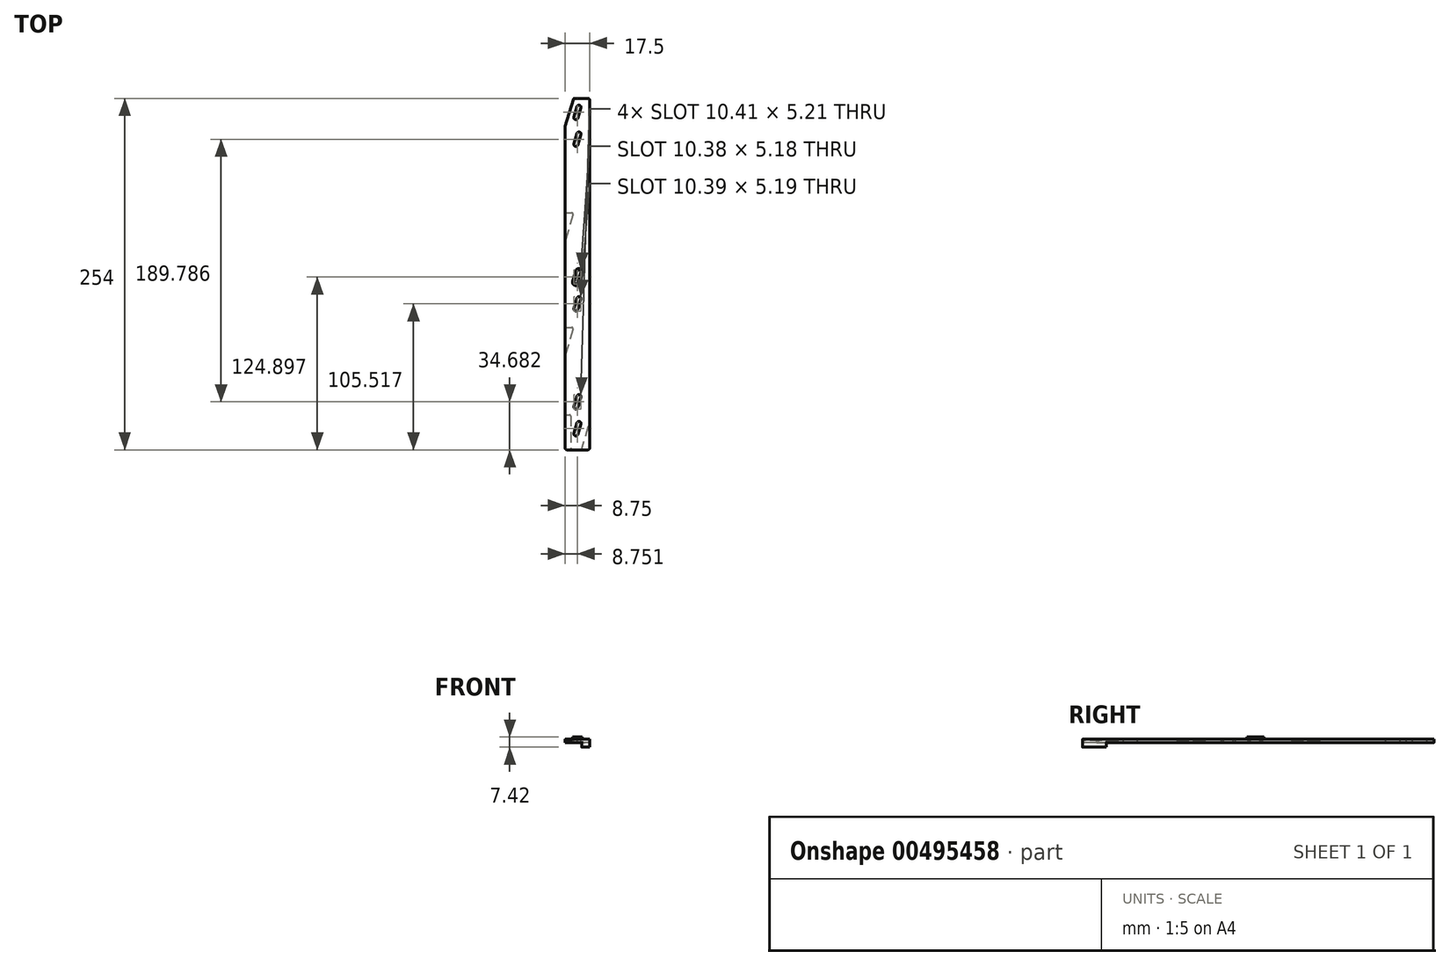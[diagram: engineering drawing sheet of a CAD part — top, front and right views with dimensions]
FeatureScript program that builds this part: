
annotation { "Feature Type Name" : "Feature", "Feature Type Description" : "" }
export const myFeature = defineFeature(function(context is Context, id is Id, definition is map)
    precondition{}
    {
        {
            var Q0;
            Q0=qCreatedBy(makeId("Top.planeOp"),FACE);
            var sketch = newSketch(context, id + "F0", { "sketchPlane" : qUnion([Q0])});
            skLineSegment(sketch, "E0.bottom", {"start": v(-2.75, 106.97) * mm, "end": v(8.75, 106.97) * mm});
            skLineSegment(sketch, "E0.left", {"start": v(-8.75, 86.96) * mm, "end": v(-8.75, -147.03) * mm});
            skLineSegment(sketch, "E0.right", {"start": v(8.75, 106.97) * mm, "end": v(8.75, -147.03) * mm});
            skLineSegment(sketch, "E1", {"start": v(-2.75, 106.97) * mm, "end": v(-8.75, 86.96) * mm});
            skLineSegment(sketch, "E2", {"start": v(-8.75, -147.03) * mm, "end": v(8.75, -147.03) * mm});
            skLineSegment(sketch, "E3", {"start": v(3, 106.97) * mm, "end": v(-14.54, 106.97) * mm, "construction": true});
            skLineSegment(sketch, "E4", {"start": v(-8.75, 86.96) * mm, "end": v(-8.75, 113.53) * mm, "construction": true});
            skSolve(sketch);
        }
        {
            var Q0;
            Q0=makeQuery(id+"F0.imprint","IMPRINT",FACE,{"disambiguationData":[TD([[makeQuery(id+"F0.imprint","IMPRINT",EDGE,{"derivedFrom":sQuery(id+"F0.wireOp",EDGE,"E0.bottom")}),-1.0]])]});
            var Q1;
            {var subQ0=sQuery(id+"F0.wireOp",EDGE,"633dc75a-0e58-463e-8379-161fb5928875");Q1=makeQuery(id+"F0.imprint","IMPRINT",FACE,{"disambiguationData":[TD([[makeQuery(id+"F0.imprint","IMPRINT",EDGE,{"derivedFrom":subQ0}),1.0]])]});}
            var Q2;
            {var subQ0=sQuery(id+"F0.wireOp",EDGE,"2a0ce6a0-4d5f-4fe7-96eb-a293c719060f");Q2=makeQuery(id+"F0.imprint","IMPRINT",FACE,{"disambiguationData":[TD([[makeQuery(id+"F0.imprint","IMPRINT",EDGE,{"derivedFrom":subQ0}),1.0]])]});}
            var Q3;
            {var subQ2=sQuery(id+"F0.wireOp",EDGE,"24cbd44b-3bb7-44ab-ab79-63d6f2c5d095");Q3=makeQuery(id+"F0.imprint","IMPRINT",FACE,{"disambiguationData":[TD([[makeQuery(id+"F0.imprint","IMPRINT",EDGE,{"derivedFrom":subQ2}),-1.0]])]});}
            var Q4;
            Q4=makeQuery(id+"F0.imprint","IMPRINT",FACE,{"disambiguationData":[TD([[makeQuery(id+"F0.imprint","IMPRINT",EDGE,{"derivedFrom":sQuery(id+"F0.wireOp",EDGE,"be87b283-c7b7-44dc-804c-dedf415bc6b7")}),1.0]])]});
            extrude(context, id + "F1", {"entities" : qUnion([Q0, Q1, Q2, Q3, Q4]), "oppositeDirection" : true, "depth" : 4.25 * mm});
        }
        {
            var Q0;
            Q0=makeQuery(id+"F1.opExtrude","CAP_FACE",FACE,{"disambiguationData":[OSD([sQuery(id+"F0.wireOp",EDGE,"E0.bottom"),sQuery(id+"F0.wireOp",EDGE,"E0.top"),sQuery(id+"F0.wireOp",EDGE,"E0.left"),sQuery(id+"F0.wireOp",EDGE,"E0.right"),sQuery(id+"F0.wireOp",EDGE,"10f6f7c6-98f3-4bf4-98ed-882440dcabe1"),sQuery(id+"F0.wireOp",EDGE,"E1"),sQuery(id+"F0.wireOp",EDGE,"7971e424-7568-4981-839e-3620bab7779a.trimOffspring"),sQuery(id+"F0.wireOp",EDGE,"998ecffa-0773-4704-a632-2820b9788bde.trimOffspring"),sQuery(id+"F0.wireOp",EDGE,"E2"),sQuery(id+"F0.wireOp",EDGE,"j7FGSntq-Wqsv-4P9R-nEKO-KN23OMY3wqPX"),sQuery(id+"F0.wireOp",EDGE,"27ecc4d9-ff6f-4d39-984e-df0c997e4436")])],"isStart":false});
            var sketch = newSketch(context, id + "F2", { "sketchPlane" : qUnion([Q0])});
            skLineSegment(sketch, "E5", {"start": v(-8.75, -24.19) * mm, "end": v(-2.75, -24.19) * mm});
            skLineSegment(sketch, "E6", {"start": v(-2.75, -24.19) * mm, "end": v(-8.75, -4.18) * mm});
            skLineSegment(sketch, "E7", {"start": v(-4.85, 147.03) * mm, "end": v(-8.75, 147.03) * mm});
            skLineSegment(sketch, "E8.trimOffspring", {"start": v(-8.75, 58.6) * mm, "end": v(-8.75, 78.6) * mm});
            skLineSegment(sketch, "E9.trimOffspring", {"start": v(-8.75, -24.19) * mm, "end": v(-8.75, -4.18) * mm});
            skLineSegment(sketch, "E10", {"start": v(-8.75, 58.6) * mm, "end": v(-2.75, 58.6) * mm});
            skLineSegment(sketch, "E11", {"start": v(-2.75, 58.6) * mm, "end": v(-8.75, 78.6) * mm});
            skLineSegment(sketch, "E12", {"start": v(-8.75, 147.03) * mm, "end": v(-8.75, 121.63) * mm});
            skLineSegment(sketch, "E13", {"start": v(-8.75, 121.63) * mm, "end": v(-4.85, 121.63) * mm});
            skLineSegment(sketch, "E14", {"start": v(-4.85, 121.63) * mm, "end": v(-4.85, 147.03) * mm});
            skLineSegment(sketch, "E15", {"start": v(-173.03, 57.3) * mm, "end": v(-173.03, 57.3) * mm});
            skLineSegment(sketch, "E16", {"start": v(8.75, 127.03) * mm, "end": v(2.75, 147.03) * mm});
            skLineSegment(sketch, "E17", {"start": v(2.75, 147.03) * mm, "end": v(8.75, 147.03) * mm});
            skLineSegment(sketch, "E18", {"start": v(8.75, 147.03) * mm, "end": v(8.75, 127.03) * mm});
            skSolve(sketch);
        }
        {
            var Q0;
            Q0=makeQuery(id+"F2.imprint","IMPRINT",FACE,{"disambiguationData":[TD([[makeQuery(id+"F2.imprint","IMPRINT",EDGE,{"derivedFrom":sQuery(id+"F2.wireOp",EDGE,"E12")}),-1.0]])]});
            var Q1;
            Q1=makeQuery(id+"F2.imprint","IMPRINT",FACE,{"disambiguationData":[TD([[makeQuery(id+"F2.imprint","IMPRINT",EDGE,{"derivedFrom":sQuery(id+"F2.wireOp",EDGE,"E8.trimOffspring")}),-1.0]])]});
            var Q2;
            Q2=makeQuery(id+"F2.imprint","IMPRINT",FACE,{"disambiguationData":[TD([[makeQuery(id+"F2.imprint","IMPRINT",EDGE,{"derivedFrom":sQuery(id+"F2.wireOp",EDGE,"E5")}),1.0]])]});
            extrude(context, id + "F3", {"entities" : qUnion([Q0, Q1, Q2]), "operationType" : NewBodyOperationType.REMOVE, "oppositeDirection" : true, "depth" : 1.7 * mm});
        }
        {
            var Q0;
            Q0=makeQuery(id+"F2.imprint","IMPRINT",FACE,{"disambiguationData":[TD([[makeQuery(id+"F2.imprint","IMPRINT",EDGE,{"derivedFrom":sQuery(id+"F2.wireOp",EDGE,"E16")}),-1.0]])]});
            extrude(context, id + "F4", {"entities" : qUnion([Q0]), "operationType" : NewBodyOperationType.ADD, "depth" : 3.17 * mm});
        }
        {
            var Q0;
            Q0=makeQuery(id+"F3.boolean.opBoolean","COPY",EDGE,{"derivedFrom":makeQuery(id+"F3.opExtrude","SWEPT_EDGE",EDGE,{"disambiguationData":[OSD([sQuery(id+"F2.wireOp",EDGE,"E10"),sQuery(id+"F2.wireOp",EDGE,"E11")])]})});
            var Q1;
            Q1=makeQuery(id+"F3.boolean.opBoolean","COPY",EDGE,{"derivedFrom":makeQuery(id+"F3.opExtrude","SWEPT_EDGE",EDGE,{"disambiguationData":[OSD([sQuery(id+"F0.wireOp",EDGE,"E0.left"),sQuery(id+"F2.wireOp",EDGE,"E8.trimOffspring"),sQuery(id+"F2.wireOp",EDGE,"E10")])]})});
            var Q2;
            Q2=makeQuery(id+"F3.boolean.opBoolean","COPY",EDGE,{"derivedFrom":makeQuery(id+"F3.opExtrude","SWEPT_EDGE",EDGE,{"disambiguationData":[OSD([sQuery(id+"F2.wireOp",EDGE,"E13"),sQuery(id+"F2.wireOp",EDGE,"E14")])]})});
            var Q3;
            Q3=makeQuery(id+"F3.boolean.opBoolean","COPY",EDGE,{"derivedFrom":makeQuery(id+"F3.opExtrude","SWEPT_EDGE",EDGE,{"disambiguationData":[OSD([sQuery(id+"F0.wireOp",EDGE,"E0.left"),sQuery(id+"F2.wireOp",EDGE,"E12"),sQuery(id+"F2.wireOp",EDGE,"E13")])]})});
            var Q4;
            Q4=makeQuery(id+"F3.boolean.opBoolean","COPY",EDGE,{"derivedFrom":makeQuery(id+"F3.opExtrude","SWEPT_EDGE",EDGE,{"disambiguationData":[OSD([sQuery(id+"F0.wireOp",EDGE,"E2"),sQuery(id+"F2.wireOp",EDGE,"E14"),sQuery(id+"F2.wireOp",EDGE,"E7")])]})});
            var Q5;
            Q5=makeQuery(id+"F1.opExtrude","SWEPT_EDGE",EDGE,{"disambiguationData":[OSD([sQuery(id+"F0.wireOp",EDGE,"E0.left"),sQuery(id+"F0.wireOp",EDGE,"E2")])]});
            var Q6;
            Q6=makeQuery(id+"F4.boolean.opBoolean","MERGE",EDGE,{"derivedFrom":[makeQuery(id+"F1.opExtrude","SWEPT_EDGE",EDGE,{"disambiguationData":[OSD([sQuery(id+"F0.wireOp",EDGE,"E0.right"),sQuery(id+"F0.wireOp",EDGE,"E2")])]}),makeQuery(id+"F4.opExtrude","SWEPT_EDGE",EDGE,{"disambiguationData":[OSD([sQuery(id+"F2.wireOp",EDGE,"E17"),sQuery(id+"F2.wireOp",EDGE,"E18")])]})]});
            var Q7;
            Q7=makeQuery(id+"F4.opExtrude","SWEPT_EDGE",EDGE,{"disambiguationData":[OSD([sQuery(id+"F0.wireOp",EDGE,"E2"),sQuery(id+"F2.wireOp",EDGE,"E16"),sQuery(id+"F2.wireOp",EDGE,"E17")])]});
            var Q8;
            Q8=makeQuery(id+"F3.boolean.opBoolean","COPY",EDGE,{"derivedFrom":makeQuery(id+"F3.opExtrude","SWEPT_EDGE",EDGE,{"disambiguationData":[OSD([sQuery(id+"F2.wireOp",EDGE,"E5"),sQuery(id+"F2.wireOp",EDGE,"E6")])]})});
            var Q9;
            Q9=makeQuery(id+"F3.boolean.opBoolean","COPY",EDGE,{"derivedFrom":makeQuery(id+"F3.opExtrude","SWEPT_EDGE",EDGE,{"disambiguationData":[OSD([sQuery(id+"F0.wireOp",EDGE,"E0.left"),sQuery(id+"F2.wireOp",EDGE,"E5"),sQuery(id+"F2.wireOp",EDGE,"E9.trimOffspring")])]})});
            var Q10;
            Q10=makeQuery(id+"F1.opExtrude","SWEPT_EDGE",EDGE,{"disambiguationData":[OSD([sQuery(id+"F0.wireOp",EDGE,"E0.bottom"),sQuery(id+"F0.wireOp",EDGE,"10f6f7c6-98f3-4bf4-98ed-882440dcabe1")])]});
            var Q11;
            Q11=makeQuery(id+"F1.opExtrude","SWEPT_EDGE",EDGE,{"disambiguationData":[OSD([sQuery(id+"F0.wireOp",EDGE,"E0.bottom"),sQuery(id+"F0.wireOp",EDGE,"E0.right")])]});
            fillet(context, id + "F5", {"entities" : qUnion([Q0, Q1, Q2, Q3, Q4, Q5, Q6, Q7, Q8, Q9, Q10, Q11]), "radius" : 1 * mm, "tangentPropagation" : true, "allowEdgeOverflow" : false});
        }
        {
            var Q0;
            Q0=makeQuery(id+"F4.opExtrude","SWEPT_EDGE",EDGE,{"disambiguationData":[OSD([sQuery(id+"F0.wireOp",EDGE,"E0.right"),sQuery(id+"F2.wireOp",EDGE,"E16"),sQuery(id+"F2.wireOp",EDGE,"E18")])]});
            fillet(context, id + "F6", {"entities" : qUnion([Q0]), "radius" : .5 * mm, "tangentPropagation" : true, "allowEdgeOverflow" : false});
        }
        {
            var Q0;
            Q0=makeQuery(id+"F0.imprint","IMPRINT",FACE,{"disambiguationData":[TD([[makeQuery(id+"F0.imprint","IMPRINT",EDGE,{"derivedFrom":sQuery(id+"F0.wireOp",EDGE,"E0.bottom")}),-1.0]])]});
            var sketch = newSketch(context, id + "F7", { "sketchPlane" : qUnion([Q0])});
            skPoint(sketch, "E19.startSnap0", {"position": v(2.87, 106.97) * mm});
            skLineSegment(sketch, "E20", {"start": v(0, 106.97) * mm, "end": v(0, -147.03) * mm, "construction": true});
            skLineSegment(sketch, "E21.MirrorCS", {"start": v(0.32, 92.68) * mm, "end": v(2.55, 100.1) * mm});
            skLineSegment(sketch, "E22.MirrorCS", {"start": v(-3.5, 93.83) * mm, "end": v(-1.28, 101.25) * mm});
            skLineSegment(sketch, "E23.MirrorCS", {"start": v(1.28, 92.4) * mm, "end": v(3.5, 99.82) * mm});
            skArc(sketch, "E24.MirrorCS", {"start": v(-2.55, 93.54) * mm, "mid": v(-1.54, 91.67) * mm, "end": v(0.32, 92.68) * mm});
            skLineSegment(sketch, "E25.MirrorCS", {"start": v(-2.55, 93.54) * mm, "end": v(-0.32, 100.97) * mm});
            skArc(sketch, "E26.MirrorCS", {"start": v(3.5, 99.82) * mm, "mid": v(1.83, 102.93) * mm, "end": v(-1.28, 101.25) * mm});
            skArc(sketch, "E27.MirrorCS", {"start": v(2.55, 100.1) * mm, "mid": v(1.54, 101.97) * mm, "end": v(-0.32, 100.97) * mm});
            skArc(sketch, "E28.MirrorCS", {"start": v(-3.5, 93.83) * mm, "mid": v(-1.83, 90.72) * mm, "end": v(1.28, 92.4) * mm});
            skArc(sketch, "E29.MirrorCS", {"start": v(1.32, -26.42) * mm, "mid": v(-1.7, -28.28) * mm, "end": v(-3.55, -25.27) * mm});
            skLineSegment(sketch, "E30.MirrorCS", {"start": v(-2.58, -25.52) * mm, "end": v(-0.35, -18.1) * mm});
            skLineSegment(sketch, "E31.MirrorCS", {"start": v(-3.55, -25.27) * mm, "end": v(-1.32, -17.84) * mm});
            skArc(sketch, "E32.MirrorCS", {"start": v(3.55, -19) * mm, "mid": v(1.7, -15.99) * mm, "end": v(-1.32, -17.84) * mm});
            skArc(sketch, "E33.MirrorCS", {"start": v(-2.58, -25.52) * mm, "mid": v(-1.44, -27.3) * mm, "end": v(0.35, -26.17) * mm});
            skArc(sketch, "E34.MirrorCS", {"start": v(2.58, -18.74) * mm, "mid": v(1.44, -16.96) * mm, "end": v(-0.35, -18.1) * mm});
            skLineSegment(sketch, "E35", {"start": v(-1.11, -25.84) * mm, "end": v(1.11, -18.42) * mm, "construction": true});
            skLineSegment(sketch, "E36.MirrorCS", {"start": v(-3.55, -44.65) * mm, "end": v(-1.32, -37.23) * mm});
            skArc(sketch, "E37.MirrorCS", {"start": v(2.57, -38.15) * mm, "mid": v(1.5, -36.36) * mm, "end": v(-0.32, -37.38) * mm});
            skLineSegment(sketch, "E38.MirrorCS", {"start": v(1.32, -45.8) * mm, "end": v(3.55, -38.39) * mm});
            skLineSegment(sketch, "E39.MirrorCS", {"start": v(0.35, -45.58) * mm, "end": v(2.57, -38.15) * mm});
            skArc(sketch, "E40.MirrorCS", {"start": v(3.55, -38.39) * mm, "mid": v(1.7, -35.37) * mm, "end": v(-1.32, -37.23) * mm});
            skArc(sketch, "E41.MirrorCS", {"start": v(-3.55, -44.65) * mm, "mid": v(-1.7, -47.66) * mm, "end": v(1.32, -45.8) * mm});
            skLineSegment(sketch, "E42.MirrorCS", {"start": v(-2.57, -44.88) * mm, "end": v(-0.32, -37.38) * mm});
            skArc(sketch, "E43.MirrorCS", {"start": v(-2.57, -44.88) * mm, "mid": v(-1.46, -46.69) * mm, "end": v(0.35, -45.58) * mm});
            skLineSegment(sketch, "E44", {"start": v(-1.11, -45.23) * mm, "end": v(1.11, -37.8) * mm, "construction": true});
            skArc(sketch, "E45.MirrorCS", {"start": v(2.55, -109.07) * mm, "mid": v(1.54, -107.2) * mm, "end": v(-0.32, -108.2) * mm});
            skArc(sketch, "E46.MirrorCS", {"start": v(-2.55, -115.63) * mm, "mid": v(-1.54, -117.5) * mm, "end": v(0.32, -116.5) * mm});
            skLineSegment(sketch, "E47.MirrorCS", {"start": v(-3.5, -115.34) * mm, "end": v(-1.28, -107.92) * mm});
            skLineSegment(sketch, "E48.MirrorCS", {"start": v(0.32, -116.5) * mm, "end": v(2.55, -109.07) * mm});
            skLineSegment(sketch, "E49.MirrorCS", {"start": v(1.28, -116.78) * mm, "end": v(3.5, -109.35) * mm});
            skLineSegment(sketch, "E50.MirrorCS", {"start": v(-2.55, -115.63) * mm, "end": v(-0.32, -108.2) * mm});
            skArc(sketch, "E51.MirrorCS", {"start": v(3.5, -109.35) * mm, "mid": v(1.83, -106.24) * mm, "end": v(-1.28, -107.92) * mm});
            skArc(sketch, "E52.MirrorCS", {"start": v(-3.5, -115.34) * mm, "mid": v(-1.83, -118.45) * mm, "end": v(1.28, -116.78) * mm});
            skLineSegment(sketch, "E53", {"start": v(-1.11, -116.06) * mm, "end": v(1.11, -108.64) * mm, "construction": true});
            skLineSegment(sketch, "E54", {"start": v(-1.11, 93.11) * mm, "end": v(1.11, 100.53) * mm, "construction": true});
            skArc(sketch, "E55.MirrorCS", {"start": v(-3.5, -134.72) * mm, "mid": v(-1.8, -137.85) * mm, "end": v(1.3, -136.1) * mm});
            skArc(sketch, "E56.MirrorCS", {"start": v(-2.56, -135.05) * mm, "mid": v(-1.55, -136.88) * mm, "end": v(0.3, -135.92) * mm});
            skLineSegment(sketch, "E57.MirrorCS", {"start": v(-3.5, -134.72) * mm, "end": v(-1.28, -127.3) * mm});
            skLineSegment(sketch, "E58.MirrorCS", {"start": v(-2.56, -135.05) * mm, "end": v(-0.33, -127.63) * mm});
            skLineSegment(sketch, "E59.MirrorCS", {"start": v(1.3, -136.1) * mm, "end": v(3.53, -128.68) * mm});
            skLineSegment(sketch, "E60.MirrorCS", {"start": v(0.3, -135.92) * mm, "end": v(2.54, -128.5) * mm});
            skArc(sketch, "E61.MirrorCS", {"start": v(3.53, -128.68) * mm, "mid": v(1.8, -125.62) * mm, "end": v(-1.28, -127.3) * mm});
            skArc(sketch, "E62.MirrorCS", {"start": v(2.54, -128.5) * mm, "mid": v(1.55, -126.58) * mm, "end": v(-0.33, -127.63) * mm});
            skLineSegment(sketch, "E63", {"start": v(1.11, -128.02) * mm, "end": v(-1.11, -135.44) * mm, "construction": true});
            skLineSegment(sketch, "E64", {"start": v(0.35, -26.17) * mm, "end": v(2.58, -18.74) * mm});
            skLineSegment(sketch, "E65", {"start": v(1.32, -26.42) * mm, "end": v(3.55, -19) * mm});
            skLineSegment(sketch, "E66.MirrorCS", {"start": v(0.32, 73.3) * mm, "end": v(2.55, 80.72) * mm});
            skLineSegment(sketch, "E67.MirrorCS", {"start": v(-3.5, 74.45) * mm, "end": v(-1.28, 81.87) * mm});
            skLineSegment(sketch, "E68.MirrorCS", {"start": v(1.28, 73) * mm, "end": v(3.5, 80.43) * mm});
            skArc(sketch, "E69.MirrorCS", {"start": v(-2.55, 74.16) * mm, "mid": v(-1.54, 72.3) * mm, "end": v(0.32, 73.3) * mm});
            skLineSegment(sketch, "E70.MirrorCS", {"start": v(-2.55, 74.16) * mm, "end": v(-0.32, 81.58) * mm});
            skArc(sketch, "E71.MirrorCS", {"start": v(3.5, 80.43) * mm, "mid": v(1.83, 83.54) * mm, "end": v(-1.28, 81.87) * mm});
            skArc(sketch, "E72.MirrorCS", {"start": v(2.55, 80.72) * mm, "mid": v(1.54, 82.59) * mm, "end": v(-0.32, 81.58) * mm});
            skArc(sketch, "E73.MirrorCS", {"start": v(-3.5, 74.45) * mm, "mid": v(-1.83, 71.33) * mm, "end": v(1.28, 73) * mm});
            skLineSegment(sketch, "E74", {"start": v(-1.11, 73.73) * mm, "end": v(1.11, 81.15) * mm, "construction": true});
            skSolve(sketch);
        }
        {
            var Q0;
            Q0=makeQuery(id+"F7.imprint","IMPRINT",FACE,{"disambiguationData":[TD([[makeQuery(id+"F7.imprint","IMPRINT",EDGE,{"derivedFrom":sQuery(id+"F7.wireOp",EDGE,"E21.MirrorCS")}),-1.0]])]});
            var Q1;
            Q1=makeQuery(id+"F7.imprint","IMPRINT",FACE,{"disambiguationData":[TD([[makeQuery(id+"F7.imprint","IMPRINT",EDGE,{"derivedFrom":sQuery(id+"F7.wireOp",EDGE,"E66.MirrorCS")}),-1.0]])]});
            var Q2;
            Q2=makeQuery(id+"F7.imprint","IMPRINT",FACE,{"disambiguationData":[TD([[makeQuery(id+"F7.imprint","IMPRINT",EDGE,{"derivedFrom":sQuery(id+"F7.wireOp",EDGE,"E36.MirrorCS")}),-1.0]])]});
            var Q3;
            Q3=makeQuery(id+"F7.imprint","IMPRINT",FACE,{"disambiguationData":[TD([[makeQuery(id+"F7.imprint","IMPRINT",EDGE,{"derivedFrom":sQuery(id+"F7.wireOp",EDGE,"E29.MirrorCS")}),-1.0]])]});
            var Q4;
            Q4=makeQuery(id+"F7.imprint","IMPRINT",FACE,{"disambiguationData":[TD([[makeQuery(id+"F7.imprint","IMPRINT",EDGE,{"derivedFrom":sQuery(id+"F7.wireOp",EDGE,"E45.MirrorCS")}),-1.0]])]});
            var Q5;
            Q5=makeQuery(id+"F7.imprint","IMPRINT",FACE,{"disambiguationData":[TD([[makeQuery(id+"F7.imprint","IMPRINT",EDGE,{"derivedFrom":sQuery(id+"F7.wireOp",EDGE,"E55.MirrorCS")}),1.0]])]});
            extrude(context, id + "F8", {"entities" : qUnion([Q0, Q1, Q2, Q3, Q4, Q5]), "operationType" : NewBodyOperationType.REMOVE, "oppositeDirection" : true, "depth" : 1.7 * mm});
        }
        {
            var Q0;
            Q0=makeQuery(id+"F7.imprint","IMPRINT",FACE,{"disambiguationData":[TD([[makeQuery(id+"F7.imprint","IMPRINT",EDGE,{"derivedFrom":sQuery(id+"F7.wireOp",EDGE,"E56.MirrorCS")}),1.0]])]});
            var Q1;
            Q1=makeQuery(id+"F7.imprint","IMPRINT",FACE,{"disambiguationData":[TD([[makeQuery(id+"F7.imprint","IMPRINT",EDGE,{"derivedFrom":sQuery(id+"F7.wireOp",EDGE,"E46.MirrorCS")}),1.0]])]});
            var Q2;
            {var subQ5=sQuery(id+"F7.wireOp",EDGE,"E42.MirrorCS");Q2=makeQuery(id+"F7.imprint","IMPRINT",FACE,{"disambiguationData":[TD([[makeQuery(id+"F7.imprint","IMPRINT",EDGE,{"derivedFrom":subQ5}),-1.0]])]});}
            var Q3;
            {var subQ5=sQuery(id+"F7.wireOp",EDGE,"E39.MirrorCS");Q3=makeQuery(id+"F7.imprint","IMPRINT",FACE,{"disambiguationData":[TD([[makeQuery(id+"F7.imprint","IMPRINT",EDGE,{"derivedFrom":subQ5}),1.0]])]});}
            var Q4;
            {var subQ5=sQuery(id+"F7.wireOp",EDGE,"e4303e23-fdbd-405b-807a-834b77a68f775.MirrorCS");Q4=makeQuery(id+"F7.imprint","IMPRINT",FACE,{"disambiguationData":[TD([[makeQuery(id+"F7.imprint","IMPRINT",EDGE,{"derivedFrom":subQ5}),1.0]])]});}
            var Q5;
            {var subQ5=sQuery(id+"F7.wireOp",EDGE,"E30.MirrorCS");Q5=makeQuery(id+"F7.imprint","IMPRINT",FACE,{"disambiguationData":[TD([[makeQuery(id+"F7.imprint","IMPRINT",EDGE,{"derivedFrom":subQ5}),-1.0]])]});}
            var Q6;
            {var subQ5=sQuery(id+"F7.wireOp",EDGE,"f3f6644c-c940-4f1d-a062-67fce6eada603.MirrorCS");Q6=makeQuery(id+"F7.imprint","IMPRINT",FACE,{"disambiguationData":[TD([[makeQuery(id+"F7.imprint","IMPRINT",EDGE,{"derivedFrom":subQ5}),1.0]])]});}
            var Q7;
            {var subQ5=sQuery(id+"F7.wireOp",EDGE,"f3f6644c-c940-4f1d-a062-67fce6eada601.MirrorCS");Q7=makeQuery(id+"F7.imprint","IMPRINT",FACE,{"disambiguationData":[TD([[makeQuery(id+"F7.imprint","IMPRINT",EDGE,{"derivedFrom":subQ5}),-1.0]])]});}
            var Q8;
            {var subQ5=sQuery(id+"F7.wireOp",EDGE,"E21.MirrorCS");Q8=makeQuery(id+"F7.imprint","IMPRINT",FACE,{"disambiguationData":[TD([[makeQuery(id+"F7.imprint","IMPRINT",EDGE,{"derivedFrom":subQ5}),1.0]])]});}
            var Q9;
            {var subQ5=sQuery(id+"F7.wireOp",EDGE,"E25.MirrorCS");Q9=makeQuery(id+"F7.imprint","IMPRINT",FACE,{"disambiguationData":[TD([[makeQuery(id+"F7.imprint","IMPRINT",EDGE,{"derivedFrom":subQ5}),-1.0]])]});}
            var Q10;
            Q10=makeQuery(id+"F7.imprint","IMPRINT",FACE,{"disambiguationData":[TD([[makeQuery(id+"F7.imprint","IMPRINT",EDGE,{"derivedFrom":sQuery(id+"F7.wireOp",EDGE,"E66.MirrorCS")}),1.0]])]});
            extrude(context, id + "F9", {"entities" : qUnion([Q0, Q1, Q2, Q3, Q4, Q5, Q6, Q7, Q8, Q9, Q10]), "operationType" : NewBodyOperationType.REMOVE, "oppositeDirection" : true, "depth" : 25 * mm});
        }
    });
